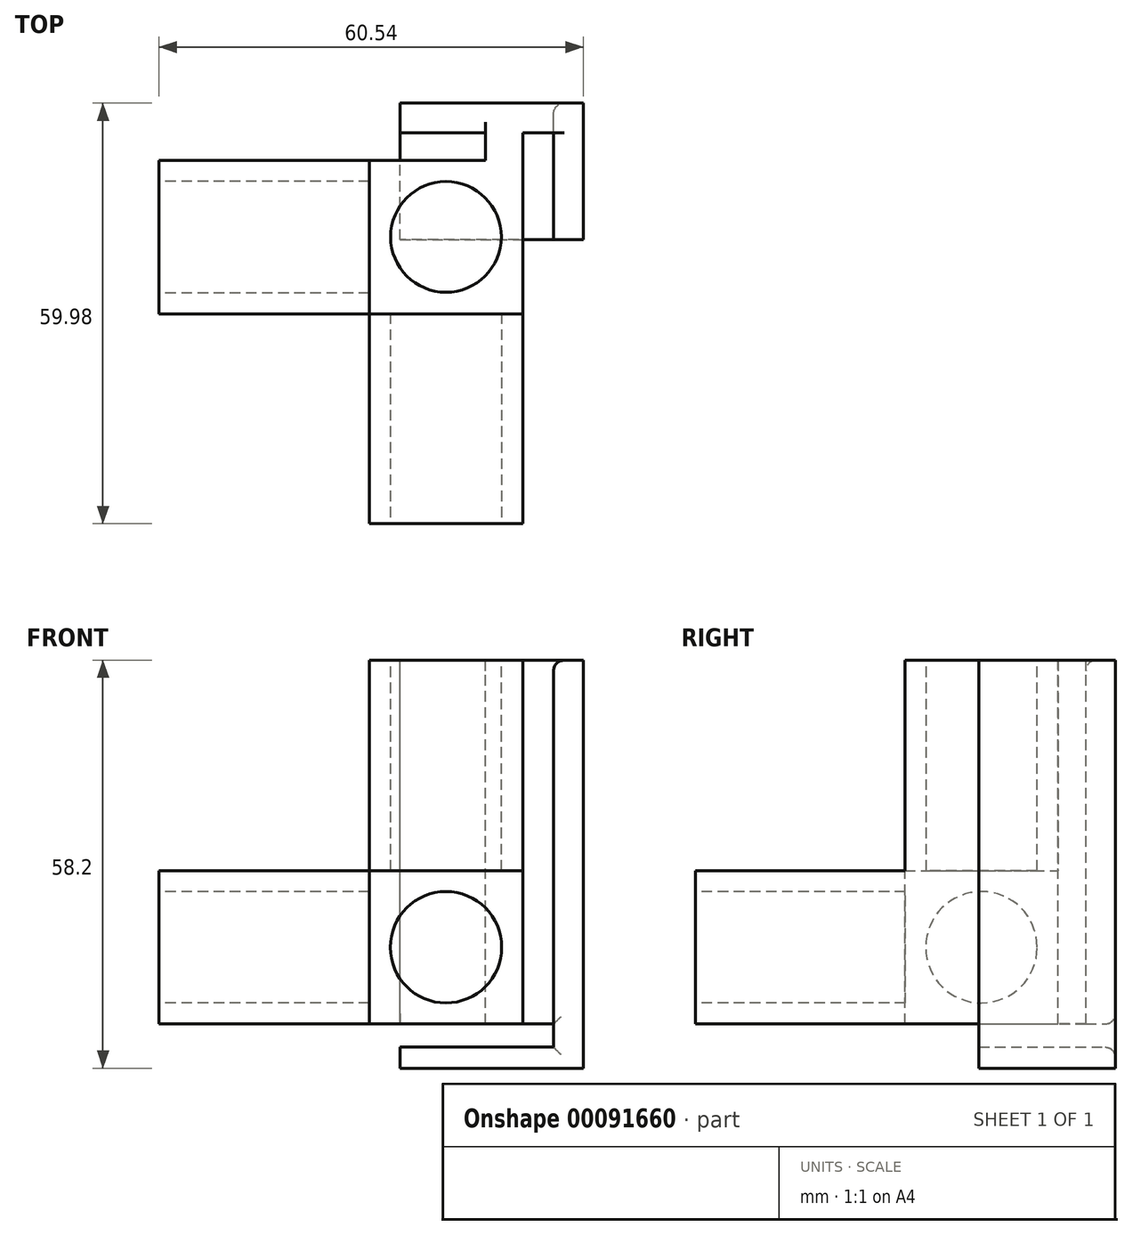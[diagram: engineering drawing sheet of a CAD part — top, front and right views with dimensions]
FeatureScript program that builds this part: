
annotation { "Feature Type Name" : "Feature", "Feature Type Description" : "" }
export const myFeature = defineFeature(function(context is Context, id is Id, definition is map)
    precondition{}
    {
        {
            var Q0;
            Q0=qCreatedBy(makeId("Front.planeOp"),FACE);
            var sketch = newSketch(context, id + "F0", { "sketchPlane" : qUnion([Q0])});
            skLineSegment(sketch, "E0.bottom", {"start": v(-42.3, 45.9) * mm, "end": v(-26.4, 45.9) * mm});
            skLineSegment(sketch, "E0.top", {"start": v(-42.3, 0) * mm, "end": v(-26.4, 0) * mm});
            skLineSegment(sketch, "E0.left", {"start": v(-42.3, 45.9) * mm, "end": v(-42.3, 0) * mm});
            skLineSegment(sketch, "E0.right", {"start": v(-26.4, 45.9) * mm, "end": v(-26.4, 15.9) * mm});
            skLineSegment(sketch, "E1.top", {"start": v(-42.3, 15.9) * mm, "end": v(-26.4, 15.9) * mm});
            skLineSegment(sketch, "E1.left", {"start": v(-42.3, 0) * mm, "end": v(-42.3, 15.9) * mm});
            skLineSegment(sketch, "E1.right", {"start": v(3.6, 0) * mm, "end": v(3.6, 15.9) * mm});
            skLineSegment(sketch, "E2", {"start": v(-26.4, 15.9) * mm, "end": v(-26.4, 0) * mm});
            skLineSegment(sketch, "E3", {"start": v(-26.4, 15.9) * mm, "end": v(3.6, 15.9) * mm});
            skLineSegment(sketch, "E4", {"start": v(-26.4, 0) * mm, "end": v(-26.4, 0) * mm});
            skLineSegment(sketch, "E5", {"start": v(-42.3, 15.9) * mm, "end": v(-42.3, 15.9) * mm});
            skLineSegment(sketch, "E6", {"start": v(-26.4, 0) * mm, "end": v(3.6, 0) * mm});
            skLineSegment(sketch, "E7.0", {"start": v(-45.3, 48.9) * mm, "end": v(-45.3, -3) * mm});
            skLineSegment(sketch, "E7.1", {"start": v(-45.3, -3) * mm, "end": v(-23.4, -3) * mm});
            skLineSegment(sketch, "E7.2", {"start": v(-23.4, 48.9) * mm, "end": v(-23.4, 18.9) * mm});
            skLineSegment(sketch, "E7.3", {"start": v(-23.4, 18.9) * mm, "end": v(6.6, 18.9) * mm});
            skLineSegment(sketch, "E7.4", {"start": v(6.6, -3) * mm, "end": v(6.6, 18.9) * mm});
            skLineSegment(sketch, "E7.5", {"start": v(-45.3, 48.9) * mm, "end": v(-23.4, 48.9) * mm});
            skLineSegment(sketch, "E7.6", {"start": v(-23.4, -3) * mm, "end": v(6.6, -3) * mm});
            skPoint(sketch, "E8", {"position": v(-34.36, 7.95) * mm});
            skPoint(sketch, "E8.positionSnap0", {"position": v(-26.4, 7.95) * mm});
            skPoint(sketch, "E8.positionSnap1", {"position": v(-34.36, 15.9) * mm});
            skCircle(sketch, "E9", {"center": v(-34.36, 7.95) * mm, "radius": 7.95 * mm});
            skLineSegment(sketch, "E10", {"start": v(-23.4, 18.9) * mm, "end": v(-45.3, 18.9) * mm});
            skLineSegment(sketch, "E11", {"start": v(-23.4, 18.9) * mm, "end": v(-23.4, -3) * mm});
            skSolve(sketch);
        }
        {
            var Q0;
            {var subQ1=sQuery(id+"F0.wireOp",EDGE,"E1.top");var subQ3=sQuery(id+"F0.wireOp",EDGE,"E9");var subQ4=makeQuery(id+"F0.imprint","INTERSECT",VERTEX,{"derivedFrom":[subQ1,subQ3]});Q0=makeQuery(id+"F0.imprint","IMPRINT",FACE,{"disambiguationData":[TD([[makeQuery(id+"F0.imprint","IMPRINT",EDGE,{"disambiguationData":[TD([[subQ4,-1.0]])],"derivedFrom":subQ3}),-1.0]])]});}
            var Q1;
            {var subQ0=sQuery(id+"F0.wireOp",EDGE,"E9");var subQ1=makeQuery(id+"F0.imprint","INTERSECT",VERTEX,{"derivedFrom":[sQuery(id+"F0.wireOp",EDGE,"E1.top"),subQ0]});Q1=makeQuery(id+"F0.imprint","IMPRINT",FACE,{"disambiguationData":[TD([[makeQuery(id+"F0.imprint","IMPRINT",EDGE,{"disambiguationData":[TD([[subQ1,1.0]])],"derivedFrom":subQ0}),1.0]])]});}
            var Q2;
            {var subQ5=sQuery(id+"F0.wireOp",EDGE,"E0.bottom");Q2=makeQuery(id+"F0.imprint","IMPRINT",FACE,{"disambiguationData":[TD([[makeQuery(id+"F0.imprint","IMPRINT",EDGE,{"derivedFrom":subQ5}),1.0]])]});}
            var Q3;
            {var subQ0=sQuery(id+"F0.wireOp",EDGE,"E1.right");Q3=makeQuery(id+"F0.imprint","IMPRINT",FACE,{"disambiguationData":[TD([[makeQuery(id+"F0.imprint","IMPRINT",EDGE,{"derivedFrom":subQ0}),1.0]])]});}
            var Q4;
            {var subQ0=sQuery(id+"F0.wireOp",EDGE,"E0.bottom");Q4=makeQuery(id+"F0.imprint","IMPRINT",FACE,{"disambiguationData":[TD([[makeQuery(id+"F0.imprint","IMPRINT",EDGE,{"derivedFrom":subQ0}),-1.0]])]});}
            var Q5;
            {var subQ0=sQuery(id+"F0.wireOp",EDGE,"E1.left");var subQ1=sQuery(id+"F0.wireOp",EDGE,"E0.top");var subQ2=makeQuery(id+"F0.imprint","INTERSECT",VERTEX,{"derivedFrom":[subQ1,subQ0]});Q5=makeQuery(id+"F0.imprint","IMPRINT",FACE,{"disambiguationData":[TD([[makeQuery(id+"F0.imprint","IMPRINT",EDGE,{"disambiguationData":[TD([[subQ2,-1.0]])],"derivedFrom":subQ1}),1.0]])]});}
            var Q6;
            {var subQ1=sQuery(id+"F0.wireOp",EDGE,"E0.top");var subQ3=sQuery(id+"F0.wireOp",EDGE,"E9");var subQ4=makeQuery(id+"F0.imprint","INTERSECT",VERTEX,{"derivedFrom":[subQ1,subQ3]});Q6=makeQuery(id+"F0.imprint","IMPRINT",FACE,{"disambiguationData":[TD([[makeQuery(id+"F0.imprint","IMPRINT",EDGE,{"disambiguationData":[TD([[subQ4,-1.0]])],"derivedFrom":subQ3}),-1.0]])]});}
            var Q7;
            {var subQ1=sQuery(id+"F0.wireOp",EDGE,"E1.top");var subQ3=sQuery(id+"F0.wireOp",EDGE,"E9");var subQ4=makeQuery(id+"F0.imprint","INTERSECT",VERTEX,{"derivedFrom":[subQ1,subQ3]});Q7=makeQuery(id+"F0.imprint","IMPRINT",FACE,{"disambiguationData":[TD([[makeQuery(id+"F0.imprint","IMPRINT",EDGE,{"disambiguationData":[TD([[subQ4,1.0]])],"derivedFrom":subQ3}),-1.0]])]});}
            var Q8;
            {var subQ5=sQuery(id+"F0.wireOp",EDGE,"E1.right");Q8=makeQuery(id+"F0.imprint","IMPRINT",FACE,{"disambiguationData":[TD([[makeQuery(id+"F0.imprint","IMPRINT",EDGE,{"derivedFrom":subQ5}),-1.0]])]});}
            var Q9;
            {var subQ4=sQuery(id+"F0.wireOp",EDGE,"E0.left");var subQ6=sQuery(id+"F0.wireOp",EDGE,"E10");var subQ8=makeQuery(id+"F0.imprint","INTERSECT",VERTEX,{"derivedFrom":[subQ4,subQ6]});Q9=makeQuery(id+"F0.imprint","IMPRINT",FACE,{"disambiguationData":[TD([[makeQuery(id+"F0.imprint","IMPRINT",EDGE,{"disambiguationData":[TD([[subQ8,1.0]])],"derivedFrom":subQ6}),1.0]])]});}
            var Q10;
            {var subQ3=sQuery(id+"F0.wireOp",EDGE,"E11");var subQ5=sQuery(id+"F0.wireOp",EDGE,"E3");var subQ8=makeQuery(id+"F0.imprint","INTERSECT",VERTEX,{"derivedFrom":[subQ5,subQ3]});Q10=makeQuery(id+"F0.imprint","IMPRINT",FACE,{"disambiguationData":[TD([[makeQuery(id+"F0.imprint","IMPRINT",EDGE,{"disambiguationData":[TD([[subQ8,-1.0]])],"derivedFrom":subQ3}),-1.0]])]});}
            var Q11;
            {var subQ14=sQuery(id+"F0.wireOp",EDGE,"E7.1");Q11=makeQuery(id+"F0.imprint","IMPRINT",FACE,{"disambiguationData":[TD([[makeQuery(id+"F0.imprint","IMPRINT",EDGE,{"derivedFrom":subQ14}),1.0]])]});}
            var Q12;
            {var subQ1=sQuery(id+"F0.wireOp",EDGE,"E0.right");var subQ3=sQuery(id+"F0.wireOp",EDGE,"E10");var subQ4=makeQuery(id+"F0.imprint","INTERSECT",VERTEX,{"derivedFrom":[subQ1,subQ3]});Q12=makeQuery(id+"F0.imprint","IMPRINT",FACE,{"disambiguationData":[TD([[makeQuery(id+"F0.imprint","IMPRINT",EDGE,{"disambiguationData":[TD([[subQ4,-1.0]])],"derivedFrom":subQ1}),1.0]])]});}
            extrude(context, id + "F1", {"entities" : qUnion([Q0, Q1, Q2, Q3, Q4, Q5, Q6, Q7, Q8, Q9, Q10, Q11, Q12]), "depth" : (15.9 + 6) * mm});
        }
        {
            var Q0;
            {var subQ14=sQuery(id+"F0.wireOp",EDGE,"E7.1");Q0=makeQuery(id+"F0.imprint","IMPRINT",FACE,{"disambiguationData":[TD([[makeQuery(id+"F0.imprint","IMPRINT",EDGE,{"derivedFrom":subQ14}),1.0]])]});}
            var Q1;
            {var subQ0=sQuery(id+"F0.wireOp",EDGE,"E9");var subQ1=makeQuery(id+"F0.imprint","INTERSECT",VERTEX,{"derivedFrom":[sQuery(id+"F0.wireOp",EDGE,"E1.top"),subQ0]});Q1=makeQuery(id+"F0.imprint","IMPRINT",FACE,{"disambiguationData":[TD([[makeQuery(id+"F0.imprint","IMPRINT",EDGE,{"disambiguationData":[TD([[subQ1,1.0]])],"derivedFrom":subQ0}),1.0]])]});}
            var Q2;
            {var subQ4=sQuery(id+"F0.wireOp",EDGE,"E0.left");var subQ6=sQuery(id+"F0.wireOp",EDGE,"E10");var subQ8=makeQuery(id+"F0.imprint","INTERSECT",VERTEX,{"derivedFrom":[subQ4,subQ6]});Q2=makeQuery(id+"F0.imprint","IMPRINT",FACE,{"disambiguationData":[TD([[makeQuery(id+"F0.imprint","IMPRINT",EDGE,{"disambiguationData":[TD([[subQ8,1.0]])],"derivedFrom":subQ6}),1.0]])]});}
            var Q3;
            {var subQ3=sQuery(id+"F0.wireOp",EDGE,"E11");var subQ5=sQuery(id+"F0.wireOp",EDGE,"E3");var subQ8=makeQuery(id+"F0.imprint","INTERSECT",VERTEX,{"derivedFrom":[subQ5,subQ3]});Q3=makeQuery(id+"F0.imprint","IMPRINT",FACE,{"disambiguationData":[TD([[makeQuery(id+"F0.imprint","IMPRINT",EDGE,{"disambiguationData":[TD([[subQ8,-1.0]])],"derivedFrom":subQ3}),-1.0]])]});}
            var Q4;
            {var subQ1=sQuery(id+"F0.wireOp",EDGE,"E0.right");var subQ3=sQuery(id+"F0.wireOp",EDGE,"E10");var subQ4=makeQuery(id+"F0.imprint","INTERSECT",VERTEX,{"derivedFrom":[subQ1,subQ3]});Q4=makeQuery(id+"F0.imprint","IMPRINT",FACE,{"disambiguationData":[TD([[makeQuery(id+"F0.imprint","IMPRINT",EDGE,{"disambiguationData":[TD([[subQ4,-1.0]])],"derivedFrom":subQ1}),1.0]])]});}
            var Q5;
            {var subQ1=sQuery(id+"F0.wireOp",EDGE,"E1.top");var subQ3=sQuery(id+"F0.wireOp",EDGE,"E9");var subQ4=makeQuery(id+"F0.imprint","INTERSECT",VERTEX,{"derivedFrom":[subQ1,subQ3]});Q5=makeQuery(id+"F0.imprint","IMPRINT",FACE,{"disambiguationData":[TD([[makeQuery(id+"F0.imprint","IMPRINT",EDGE,{"disambiguationData":[TD([[subQ4,1.0]])],"derivedFrom":subQ3}),-1.0]])]});}
            var Q6;
            {var subQ1=sQuery(id+"F0.wireOp",EDGE,"E1.top");var subQ3=sQuery(id+"F0.wireOp",EDGE,"E9");var subQ4=makeQuery(id+"F0.imprint","INTERSECT",VERTEX,{"derivedFrom":[subQ1,subQ3]});Q6=makeQuery(id+"F0.imprint","IMPRINT",FACE,{"disambiguationData":[TD([[makeQuery(id+"F0.imprint","IMPRINT",EDGE,{"disambiguationData":[TD([[subQ4,-1.0]])],"derivedFrom":subQ3}),-1.0]])]});}
            var Q7;
            {var subQ0=sQuery(id+"F0.wireOp",EDGE,"E1.left");var subQ1=sQuery(id+"F0.wireOp",EDGE,"E0.top");var subQ2=makeQuery(id+"F0.imprint","INTERSECT",VERTEX,{"derivedFrom":[subQ1,subQ0]});Q7=makeQuery(id+"F0.imprint","IMPRINT",FACE,{"disambiguationData":[TD([[makeQuery(id+"F0.imprint","IMPRINT",EDGE,{"disambiguationData":[TD([[subQ2,-1.0]])],"derivedFrom":subQ1}),1.0]])]});}
            var Q8;
            {var subQ1=sQuery(id+"F0.wireOp",EDGE,"E0.top");var subQ3=sQuery(id+"F0.wireOp",EDGE,"E9");var subQ4=makeQuery(id+"F0.imprint","INTERSECT",VERTEX,{"derivedFrom":[subQ1,subQ3]});Q8=makeQuery(id+"F0.imprint","IMPRINT",FACE,{"disambiguationData":[TD([[makeQuery(id+"F0.imprint","IMPRINT",EDGE,{"disambiguationData":[TD([[subQ4,-1.0]])],"derivedFrom":subQ3}),-1.0]])]});}
            extrude(context, id + "F2", {"entities" : qUnion([Q0, Q1, Q2, Q3, Q4, Q5, Q6, Q7, Q8]), "operationType" : NewBodyOperationType.ADD, "depth" : (15.8 + 6 + 30) * mm});
        }
        {
            var Q0;
            Q0=makeQuery(id+"F2.opExtrude","CAP_FACE",FACE,{"disambiguationData":[OSD([sQuery(id+"F0.wireOp",EDGE,"E7.0"),sQuery(id+"F0.wireOp",EDGE,"E7.1"),sQuery(id+"F0.wireOp",EDGE,"E10"),sQuery(id+"F0.wireOp",EDGE,"E11")])],"isStart":false});
            var sketch = newSketch(context, id + "F3", { "sketchPlane" : qUnion([Q0])});
            skCircle(sketch, "E12.0", {"center": v(-34.36, 7.95) * mm, "radius": 7.95 * mm});
            skSolve(sketch);
        }
        {
            var Q0;
            Q0=makeQuery(id+"F1.opExtrude","SWEPT_FACE",FACE,{"disambiguationData":[OSD([sQuery(id+"F0.wireOp",EDGE,"E7.5")])]});
            var sketch = newSketch(context, id + "F4", { "sketchPlane" : qUnion([Q0])});
            skPoint(sketch, "E13", {"position": v(-34.36, -3) * mm});
            skPoint(sketch, "E14", {"position": v(-26.4, -10.9) * mm});
            skPoint(sketch, "E15", {"position": v(-34.36, -10.9) * mm});
            skPoint(sketch, "E16", {"position": v(-62.98, 75) * mm});
            skPoint(sketch, "E17.orphan", {"position": v(-42.3, -3) * mm});
            skPoint(sketch, "E18.orphan", {"position": v(-26.4, -3) * mm});
            skPoint(sketch, "E19.orphan", {"position": v(-26.4, -18.8) * mm});
            skCircle(sketch, "E20", {"center": v(-34.36, -10.9) * mm, "radius": 7.9 * mm});
            skSolve(sketch);
        }
        {
            var Q0;
            Q0=makeQuery(id+"F1.opExtrude","SWEPT_FACE",FACE,{"disambiguationData":[OSD([sQuery(id+"F0.wireOp",EDGE,"E7.4")])]});
            var sketch = newSketch(context, id + "F5", { "sketchPlane" : qUnion([Q0])});
            skLineSegment(sketch, "E21.0", {"start": v(-18.9, 15.9) * mm, "end": v(-3, 15.9) * mm});
            skLineSegment(sketch, "E21.1", {"start": v(-18.9, 0) * mm, "end": v(-18.9, 15.9) * mm});
            skLineSegment(sketch, "E21.2", {"start": v(-18.9, 0) * mm, "end": v(-3, 0) * mm});
            skLineSegment(sketch, "E21.3", {"start": v(-3, 0) * mm, "end": v(-3, 15.9) * mm});
            skCircle(sketch, "E22", {"center": v(-10.95, 7.95) * mm, "radius": 7.95 * mm});
            skPoint(sketch, "E22.centerSnap0", {"position": v(-10.95, 0) * mm});
            skPoint(sketch, "E22.centerSnap1", {"position": v(-3, 7.95) * mm});
            skSolve(sketch);
        }
        {
            var Q0;
            Q0=makeQuery(id+"F3.imprint","IMPRINT",FACE,{"disambiguationData":[TD([[makeQuery(id+"F3.imprint","IMPRINT",EDGE,{"derivedFrom":sQuery(id+"F3.wireOp",EDGE,"E12.0")}),1.0]])]});
            extrude(context, id + "F6", {"entities" : qUnion([Q0]), "operationType" : NewBodyOperationType.REMOVE, "oppositeDirection" : true, "depth" : 30 * mm});
        }
        {
            var Q0;
            {var subQ0=sQuery(id+"F5.wireOp",EDGE,"E22");var subQ1=makeQuery(id+"F5.imprint","INTERSECT",VERTEX,{"derivedFrom":[sQuery(id+"F5.wireOp",EDGE,"E21.1"),subQ0]});Q0=makeQuery(id+"F5.imprint","IMPRINT",FACE,{"disambiguationData":[TD([[makeQuery(id+"F5.imprint","IMPRINT",EDGE,{"disambiguationData":[TD([[subQ1,1.0]])],"derivedFrom":subQ0}),1.0]])]});}
            extrude(context, id + "F7", {"entities" : qUnion([Q0]), "operationType" : NewBodyOperationType.REMOVE, "oppositeDirection" : true, "depth" : 30 * mm});
        }
        {
            var Q0;
            Q0=makeQuery(id+"F4.imprint","IMPRINT",FACE,{"disambiguationData":[TD([[makeQuery(id+"F4.imprint","IMPRINT",EDGE,{"derivedFrom":sQuery(id+"F4.wireOp",EDGE,"E20")}),1.0]])]});
            var Q1;
            Q1=sQuery(id+"F4.wireOp",EDGE,"E20");
            extrude(context, id + "F8", {"entities" : qUnion([Q0]), "operationType" : NewBodyOperationType.REMOVE, "surfaceEntities" : qUnion([Q1]), "oppositeDirection" : true, "depth" : 30 * mm});
        }
        {
            assignVariable(context, id + "F9", {"name" : "extrude", "anyValue" : 6 + 15.9 + 30});
        }
        {
            var Q0;
            Q0=makeQuery(id+"F1.opExtrude","SWEPT_FACE",FACE,{"disambiguationData":[OSD([sQuery(id+"F0.wireOp",EDGE,"E7.5")])]});
            var sketch = newSketch(context, id + "F10", { "sketchPlane" : qUnion([Q0])});
            skLineSegment(sketch, "E23", {"start": v(-45.3, 0) * mm, "end": v(-45.3, 8.18) * mm});
            skLineSegment(sketch, "E24", {"start": v(-45.3, 8.18) * mm, "end": v(-27.83, 8.18) * mm});
            skLineSegment(sketch, "E25", {"start": v(-27.83, 8.18) * mm, "end": v(-27.83, 3.95) * mm});
            skLineSegment(sketch, "E26", {"start": v(-27.83, 3.95) * mm, "end": v(-39.97, 3.95) * mm});
            skLineSegment(sketch, "E27", {"start": v(-39.97, 3.95) * mm, "end": v(-39.97, 0) * mm});
            skLineSegment(sketch, "E28", {"start": v(-45.3, 8.18) * mm, "end": v(-53.95, 8.18) * mm});
            skLineSegment(sketch, "E29", {"start": v(-53.95, 8.18) * mm, "end": v(-53.95, -11.32) * mm});
            skLineSegment(sketch, "E30", {"start": v(-53.95, -11.32) * mm, "end": v(-49.72, -11.32) * mm});
            skLineSegment(sketch, "E31", {"start": v(-49.72, -11.32) * mm, "end": v(-49.72, 3.95) * mm});
            skLineSegment(sketch, "E32", {"start": v(-49.72, 3.95) * mm, "end": v(-45.3, 3.95) * mm});
            skLineSegment(sketch, "E33", {"start": v(-49.72, 3.95) * mm, "end": v(-49.72, 8.18) * mm});
            skSolve(sketch);
        }
        {
            var Q0;
            {var subQ0=sQuery(id+"F10.wireOp",EDGE,"E29");Q0=makeQuery(id+"F10.imprint","IMPRINT",FACE,{"disambiguationData":[TD([[makeQuery(id+"F10.imprint","IMPRINT",EDGE,{"derivedFrom":subQ0}),1.0]])]});}
            var Q1;
            {var subQ3=sQuery(id+"F10.wireOp",EDGE,"E32");Q1=makeQuery(id+"F10.imprint","IMPRINT",FACE,{"disambiguationData":[TD([[makeQuery(id+"F10.imprint","IMPRINT",EDGE,{"derivedFrom":subQ3}),1.0]])]});}
            var Q2;
            {var subQ0=sQuery(id+"F10.wireOp",EDGE,"E24");Q2=makeQuery(id+"F10.imprint","IMPRINT",FACE,{"disambiguationData":[TD([[makeQuery(id+"F10.imprint","IMPRINT",EDGE,{"derivedFrom":subQ0}),-1.0]])]});}
            extrude(context, id + "F11", {"entities" : qUnion([Q0, Q1, Q2]), "operationType" : NewBodyOperationType.ADD, "oppositeDirection" : true, "depth" : (getVariable(context, 'extrude')) * mm});
        }
        {
            var Q0;
            {var subQ0=sQuery(id+"F0.wireOp",EDGE,"E7.1");Q0=makeQuery(id+"F11.boolean.opBoolean","MERGE",FACE,{"derivedFrom":[makeQuery(id+"F2.boolean.opBoolean","MERGE",FACE,{"derivedFrom":[makeQuery(id+"F1.opExtrude","SWEPT_FACE",FACE,{"disambiguationData":[OSD([subQ0,sQuery(id+"F0.wireOp",EDGE,"E7.6")])]}),makeQuery(id+"F2.opExtrude","SWEPT_FACE",FACE,{"disambiguationData":[OSD([subQ0])]})]}),makeQuery(id+"F11.opExtrude","CAP_FACE",FACE,{"disambiguationData":[OSD([sQuery(id+"F0.wireOp",EDGE,"E7.5"),sQuery(id+"F10.wireOp",EDGE,"E23"),sQuery(id+"F10.wireOp",EDGE,"E24"),sQuery(id+"F10.wireOp",EDGE,"E25"),sQuery(id+"F10.wireOp",EDGE,"E26"),sQuery(id+"F10.wireOp",EDGE,"E27"),sQuery(id+"F10.wireOp",EDGE,"E28"),sQuery(id+"F10.wireOp",EDGE,"E29"),sQuery(id+"F10.wireOp",EDGE,"E30"),sQuery(id+"F10.wireOp",EDGE,"E31"),sQuery(id+"F10.wireOp",EDGE,"E32")])],"isStart":false})]});}
            var sketch = newSketch(context, id + "F12", { "sketchPlane" : qUnion([Q0])});
            skLineSegment(sketch, "E34.0.0", {"start": v(6.6, 21.9) * mm, "end": v(-23.4, 21.9) * mm});
            skLineSegment(sketch, "E34.0.1", {"start": v(-23.4, 21.9) * mm, "end": v(-23.4, 51.8) * mm});
            skLineSegment(sketch, "E34.0.2", {"start": v(-23.4, 51.8) * mm, "end": v(-45.3, 51.8) * mm});
            skLineSegment(sketch, "E34.0.3", {"start": v(-45.3, 51.8) * mm, "end": v(-45.3, -3.95) * mm});
            skLineSegment(sketch, "E34.0.4", {"start": v(-45.3, -3.95) * mm, "end": v(-49.72, -3.95) * mm});
            skLineSegment(sketch, "E34.0.5", {"start": v(-49.72, -3.95) * mm, "end": v(-49.72, 11.32) * mm});
            skLineSegment(sketch, "E34.0.6", {"start": v(-49.72, 11.32) * mm, "end": v(-53.95, 11.32) * mm});
            skLineSegment(sketch, "E34.0.7", {"start": v(-53.95, 11.32) * mm, "end": v(-53.95, -8.18) * mm});
            skLineSegment(sketch, "E34.0.8", {"start": v(-53.95, -8.18) * mm, "end": v(-27.83, -8.18) * mm});
            skLineSegment(sketch, "E34.0.9", {"start": v(-27.83, -8.18) * mm, "end": v(-27.83, -3.95) * mm});
            skLineSegment(sketch, "E34.0.10", {"start": v(-27.83, -3.95) * mm, "end": v(-39.97, -3.95) * mm});
            skLineSegment(sketch, "E34.0.11", {"start": v(-39.97, -3.95) * mm, "end": v(-39.97, 0) * mm});
            skLineSegment(sketch, "E34.0.12", {"start": v(-39.97, 0) * mm, "end": v(6.6, 0) * mm});
            skLineSegment(sketch, "E34.0.13", {"start": v(6.6, 0) * mm, "end": v(6.6, 21.9) * mm});
            skLineSegment(sketch, "E35", {"start": v(-49.72, -3.95) * mm, "end": v(-49.72, -8.18) * mm});
            skSolve(sketch);
        }
        {
            var Q0;
            Q0=makeQuery(id+"F12.imprint","IMPRINT",FACE,{"disambiguationData":[TD([[makeQuery(id+"F12.imprint","IMPRINT",EDGE,{"derivedFrom":sQuery(id+"F12.wireOp",EDGE,"E34.0.5")}),-1.0]])]});
            extrude(context, id + "F13", {"entities" : qUnion([Q0]), "operationType" : NewBodyOperationType.ADD, "depth" : 6.3 * mm});
        }
        {
            var Q0;
            Q0=makeQuery(id+"F13.boolean.opBoolean","MERGE",FACE,{"derivedFrom":[makeQuery(id+"F11.opExtrude","SWEPT_FACE",FACE,{"disambiguationData":[OSD([sQuery(id+"F10.wireOp",EDGE,"E29")])]}),makeQuery(id+"F13.opExtrude","SWEPT_FACE",FACE,{"disambiguationData":[OSD([sQuery(id+"F12.wireOp",EDGE,"E34.0.7")])]})]});
            var sketch = newSketch(context, id + "F14", { "sketchPlane" : qUnion([Q0])});
            skLineSegment(sketch, "E36.0.0", {"start": v(11.32, 48.9) * mm, "end": v(-8.18, 48.9) * mm});
            skLineSegment(sketch, "E36.0.1", {"start": v(-8.18, 48.9) * mm, "end": v(-8.18, -9.3) * mm});
            skLineSegment(sketch, "E36.0.2", {"start": v(-8.18, -9.3) * mm, "end": v(11.32, -9.3) * mm});
            skLineSegment(sketch, "E36.0.3", {"start": v(11.32, -9.3) * mm, "end": v(11.32, 48.9) * mm});
            skLineSegment(sketch, "E37", {"start": v(-8.18, -6.3) * mm, "end": v(11.32, -6.3) * mm});
            skSolve(sketch);
        }
        {
            var Q0;
            {var subQ0=sQuery(id+"F14.wireOp",EDGE,"E36.0.2");Q0=makeQuery(id+"F14.imprint","IMPRINT",FACE,{"disambiguationData":[TD([[makeQuery(id+"F14.imprint","IMPRINT",EDGE,{"derivedFrom":subQ0}),1.0]])]});}
            var Q1;
            Q1=makeQuery(id+"F11.opExtrude","SWEPT_FACE",FACE,{"disambiguationData":[OSD([sQuery(id+"F10.wireOp",EDGE,"E25")])]});
            extrude(context, id + "F15", {"entities" : qUnion([Q0]), "operationType" : NewBodyOperationType.ADD, "endBound" : BoundingType.UP_TO_SURFACE, "oppositeDirection" : true, "endBoundEntityFace" : qUnion([Q1]), "depth" : 25 * mm});
        }
        {
            var Q0;
            Q0=makeQuery(id+"F15.opExtrude","SWEPT_EDGE",EDGE,{"disambiguationData":[OSD([sQuery(id+"F14.wireOp",EDGE,"E36.0.1"),sQuery(id+"F14.wireOp",EDGE,"E37")])]});
            var Q1;
            Q1=makeQuery(id+"F11.opExtrude","CAP_EDGE",EDGE,{"disambiguationData":[OSD([sQuery(id+"F10.wireOp",EDGE,"E24"),sQuery(id+"F10.wireOp",EDGE,"E28")])],"isStart":false});
            var Q2;
            Q2=makeQuery(id+"F11.opExtrude","CAP_EDGE",EDGE,{"disambiguationData":[OSD([sQuery(id+"F10.wireOp",EDGE,"E26")])],"isStart":true});
            var Q3;
            Q3=makeQuery(id+"F11.opExtrude","CAP_EDGE",EDGE,{"disambiguationData":[OSD([sQuery(id+"F10.wireOp",EDGE,"E31")])],"isStart":true});
            var Q4;
            Q4=makeQuery(id+"F13.opExtrude","SWEPT_EDGE",EDGE,{"disambiguationData":[OSD([sQuery(id+"F12.wireOp",EDGE,"E34.0.8"),sQuery(id+"F12.wireOp",EDGE,"E35")])]});
            fillet(context, id + "F16", {"entities" : qUnion([Q0, Q1, Q2, Q3, Q4]), "radius" : 1.5 * mm, "tangentPropagation" : true, "allowEdgeOverflow" : false});
        }
        {
            var Q0;
            Q0=makeQuery(id+"F1.opExtrude","SWEPT_BODY",BODY,{"disambiguationData":[OSD([sQuery(id+"F0.wireOp",EDGE,"E7.0"),sQuery(id+"F0.wireOp",EDGE,"E7.1"),sQuery(id+"F0.wireOp",EDGE,"E7.2"),sQuery(id+"F0.wireOp",EDGE,"E7.3"),sQuery(id+"F0.wireOp",EDGE,"E7.4"),sQuery(id+"F0.wireOp",EDGE,"E7.5"),sQuery(id+"F0.wireOp",EDGE,"E7.6")])]});
            var Q1;
            Q1=makeQuery(id+"F1.opExtrude","SWEPT_FACE",FACE,{"disambiguationData":[OSD([sQuery(id+"F0.wireOp",EDGE,"E7.4")])]});
            mirror(context, id + "F17", {"entities" : qUnion([Q0]), "mirrorPlane" : qUnion([Q1])});
        }
        {
            var Q0;
            Q0=makeQuery(id+"F1.opExtrude","SWEPT_BODY",BODY,{"disambiguationData":[OSD([sQuery(id+"F0.wireOp",EDGE,"E7.0"),sQuery(id+"F0.wireOp",EDGE,"E7.1"),sQuery(id+"F0.wireOp",EDGE,"E7.2"),sQuery(id+"F0.wireOp",EDGE,"E7.3"),sQuery(id+"F0.wireOp",EDGE,"E7.4"),sQuery(id+"F0.wireOp",EDGE,"E7.5"),sQuery(id+"F0.wireOp",EDGE,"E7.6")])]});
            deleteBodies(context, id + "F18", {"entities" : qUnion([Q0])});
        }
    });
